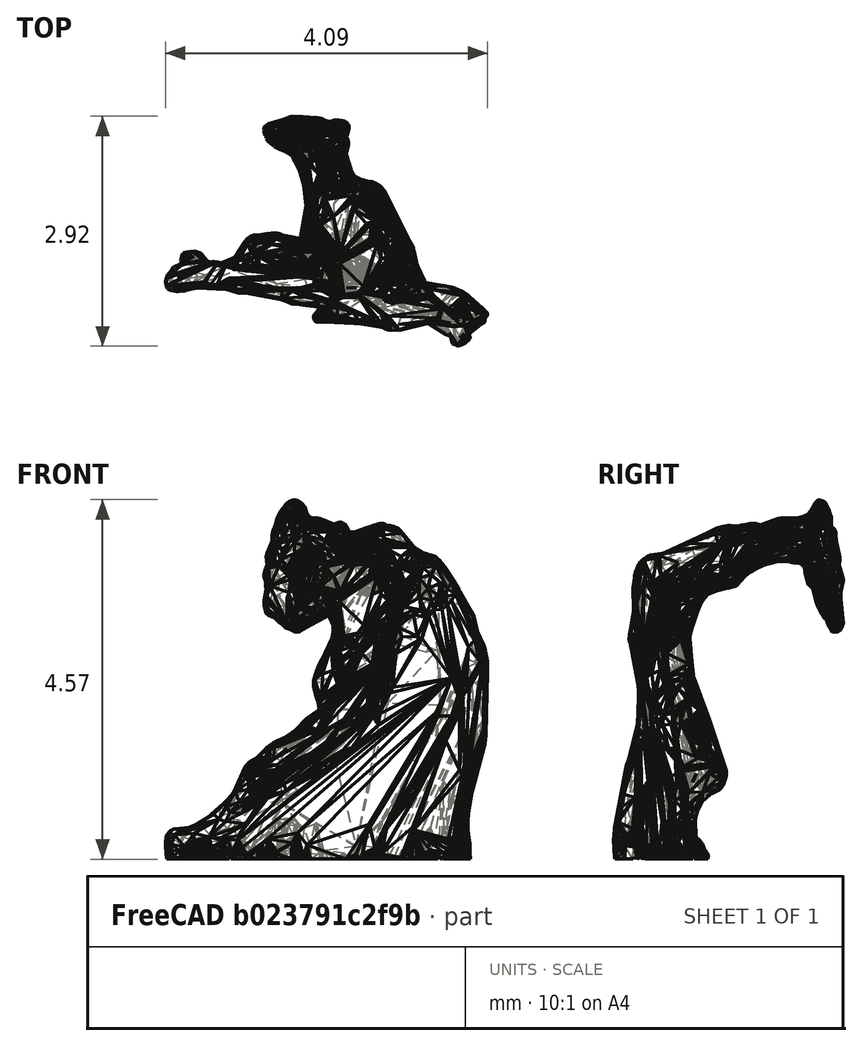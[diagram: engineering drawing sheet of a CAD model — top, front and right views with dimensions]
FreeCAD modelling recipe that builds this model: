
FCSTD DOCUMENT  (FreeCAD 0.20R29603 (Git))
Label: pwp
License: All rights reserved
LicenseURL: http://en.wikipedia.org/wiki/All_rights_reserved
objects: Mesh::Feature×2, Part::Feature×2, PartDesign::FeatureBase×1, PartDesign::Plane×1, Sketcher::SketchObject×1, PartDesign::Line×1, PartDesign::Point×1, PartDesign::Body×1
note: 8 computed .brp shape members not serialized (recipe doc carries the construction recipe); baked Part::Feature solids carry a one-line shape summary decoded from their .brp

FEATURE [Mesh::Feature] pwp
FEATURE [Part::Feature] pwp001
  shape: bbox 4.093 x 2.918 x 4.562 mm, 7946 faces, 0 solids (baked)
FEATURE [Part::Feature] pwp001_solid  label="pwp001 (Solid)"
  shape: bbox 4.093 x 2.918 x 4.562 mm, 7946 faces (baked)
FEATURE [PartDesign::FeatureBase] BaseFeature
  BaseFeature = -> pwp001
FEATURE [PartDesign::Plane] DatumPlane
  AttachmentOffset = pos=(0,0,-2.4) rot=(0,0,1;0rad)
  Length = 60
  MapMode = 5
  Placement = pos=(0,2.4,5e-16) rot=(1,0,0;1.5708rad)
  ResizeMode = 0
  Support = -> [XZ_Plane]
  Width = 60
FEATURE [Sketcher::SketchObject] Sketch  label="ii_sclerite_axis_Sketch"
  FullyConstrained = true
  MapMode = 5
  Placement = pos=(0,2.4,5e-16) rot=(0,0.707107,0.707107;3.14159rad)
  Support = -> [DatumPlane]
  sketch-geometry (2):
    g0: LineSegment StartX=-3.34474 StartY=13.2049 StartZ=0 EndX=2.86123 EndY=9.33427 EndZ=0
    g1: GeomPoint X=0 Y=11.1188 Z=0
  constraints (6):
    c: DistanceX(g0) = 2.86123
    c: DistanceY(g0) = 9.33427
    c: DistanceX(g0) = -3.34474
    c: DistanceY(g0) = 13.2049
    c: PointOnObject(g1,g0)
    c: PointOnObject(g1,g-2)
FEATURE [Mesh::Feature] ii_sclerite
FEATURE [PartDesign::Line] DatumLine  label="ii_sclerite_axis_DatumLine"
  AttacherType = Attacher::AttachEngineLine
  Length = 20
  MapMode = 29
  Placement = pos=(-4.99265,2.4,8.00489) rot=(-0.658255,0.658255,0.365239;3.84196rad)
  ResizeMode = 0
  Support = -> [Sketch]
FEATURE [PartDesign::Point] DatumPoint  label="ii_sclerite_axis_DatumPoint"
  AttacherType = Attacher::AttachEnginePoint
  MapMode = 37
  Placement = pos=(0,2.4,11.1188) rot=(0,0,1;0rad)
  Support = -> [Sketch]
FEATURE [PartDesign::Body] Body  label="pwp_Body"
  BaseFeature = -> pwp001
  Group = -> [BaseFeature,DatumPlane,Sketch,DatumLine,DatumPoint]
  Origin = -> Origin
  Tip = -> BaseFeature
